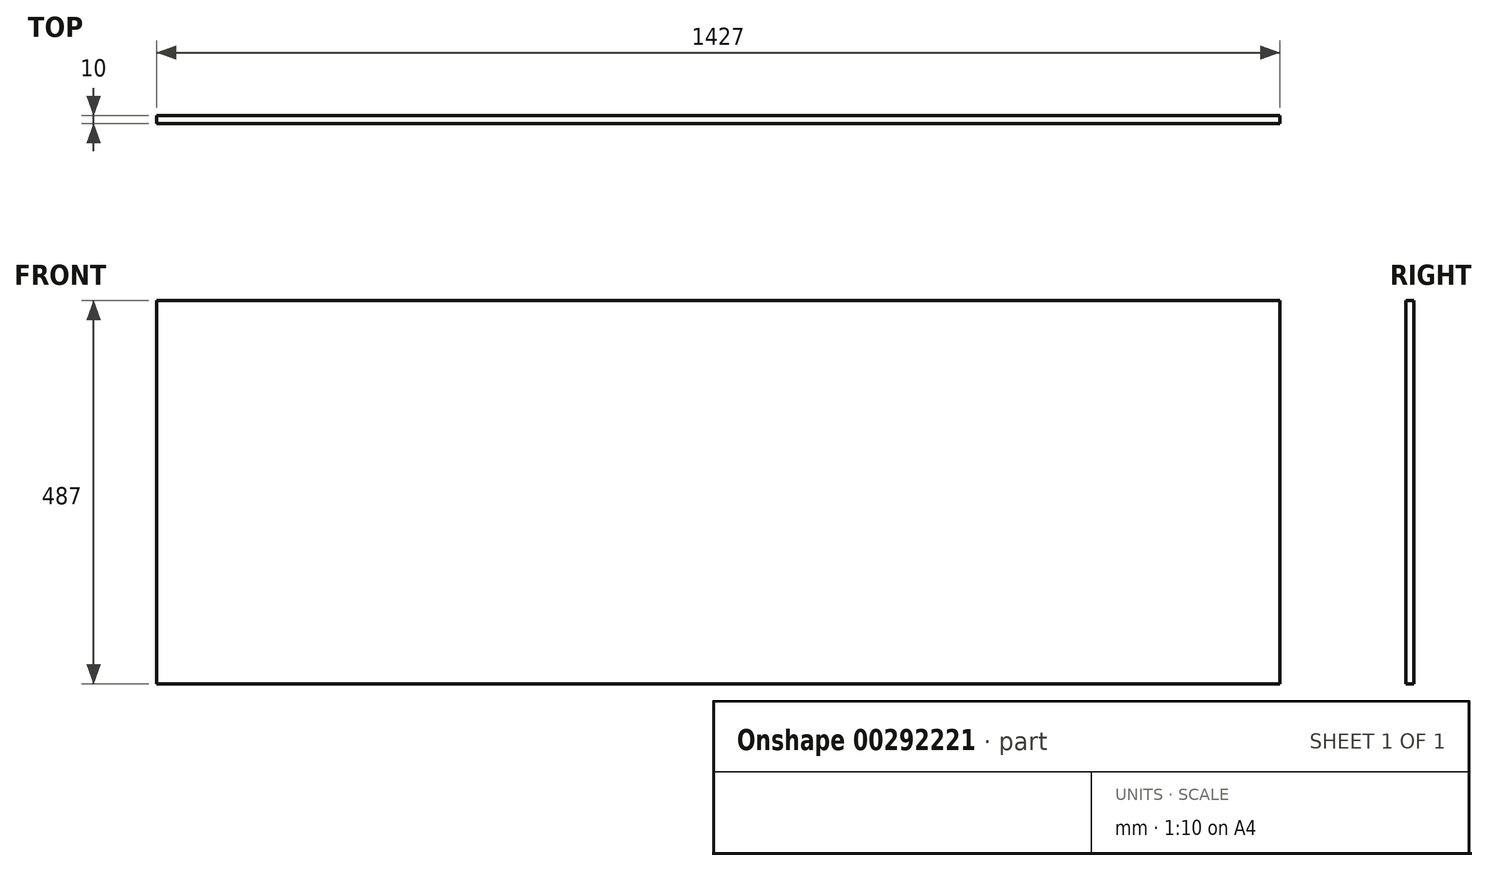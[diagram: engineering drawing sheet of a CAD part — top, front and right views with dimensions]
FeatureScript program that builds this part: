
annotation { "Feature Type Name" : "Feature", "Feature Type Description" : "" }
export const myFeature = defineFeature(function(context is Context, id is Id, definition is map)
    precondition{}
    {
        {
            var Q0;
            Q0=qCreatedBy(makeId("Front.planeOp"),FACE);
            var sketch = newSketch(context, id + "F0", { "sketchPlane" : qUnion([Q0])});
            skLineSegment(sketch, "E0.bottom", {"start": v(-713.5, 243.5) * mm, "end": v(713.5, 243.5) * mm});
            skLineSegment(sketch, "E0.top", {"start": v(-713.5, -243.5) * mm, "end": v(713.5, -243.5) * mm});
            skLineSegment(sketch, "E0.left", {"start": v(-713.5, 243.5) * mm, "end": v(-713.5, -243.5) * mm});
            skLineSegment(sketch, "E0.right", {"start": v(713.5, 243.5) * mm, "end": v(713.5, -243.5) * mm});
            skPoint(sketch, "E0.middle", {"position": v(0, 0) * mm});
            skSolve(sketch);
        }
        {
            var Q0;
            Q0 = qSketchRegion(id + "F0", true);
            extrude(context, id + "F1", {"entities" : qUnion([Q0]), "depth" : 10 * mm});
        }
    });
